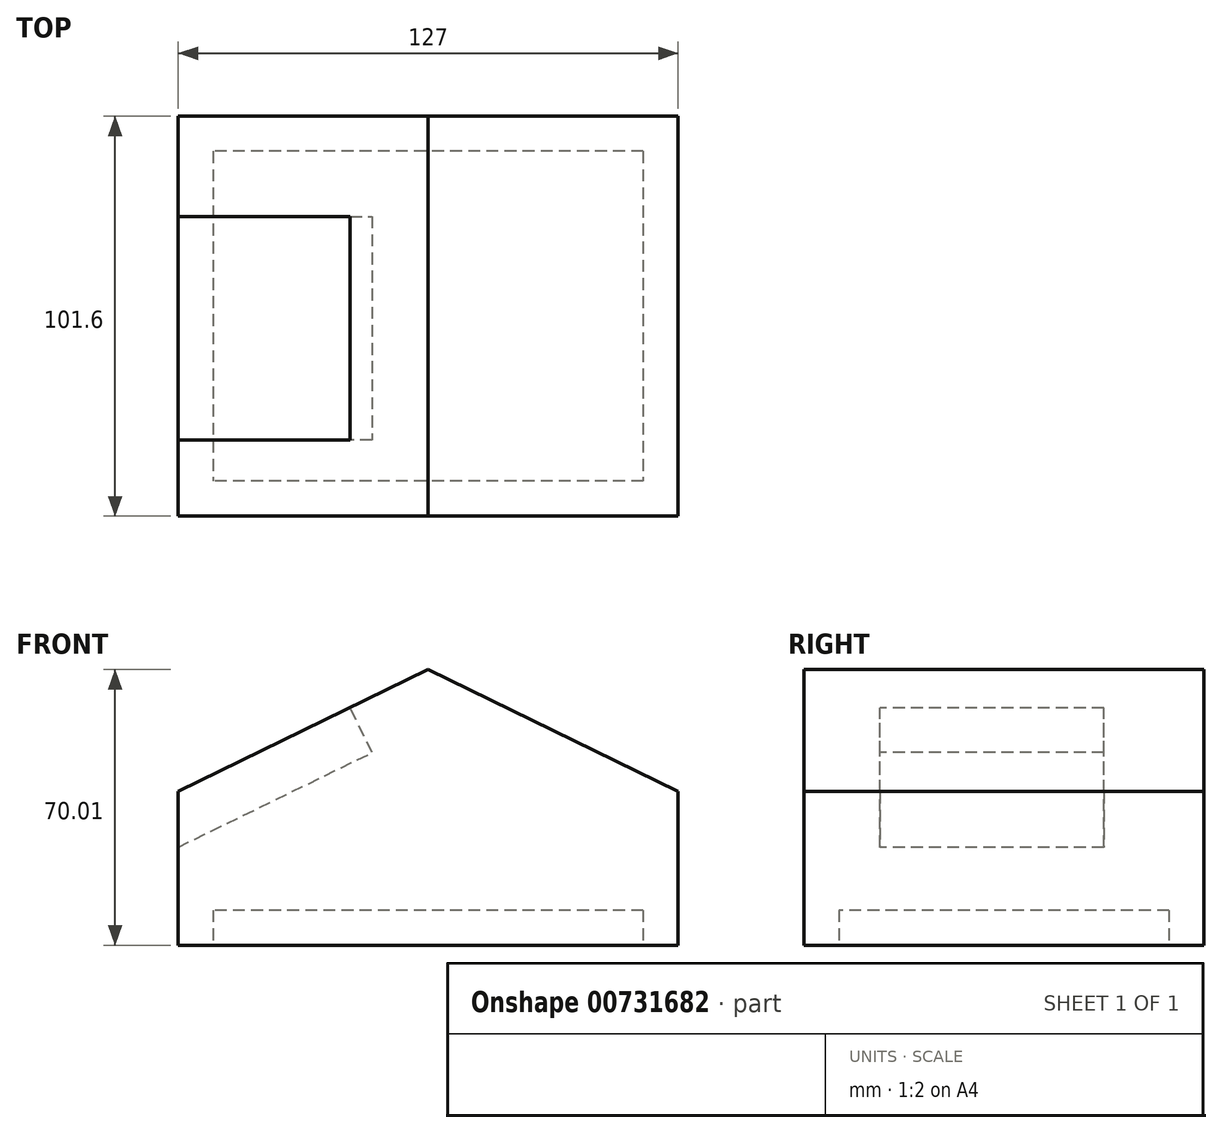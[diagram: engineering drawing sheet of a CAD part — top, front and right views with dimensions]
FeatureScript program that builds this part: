
annotation { "Feature Type Name" : "Feature", "Feature Type Description" : "" }
export const myFeature = defineFeature(function(context is Context, id is Id, definition is map)
    precondition{}
    {
        {
            var Q0;
            Q0=qCreatedBy(makeId("Right.planeOp"),FACE);
            var sketch = newSketch(context, id + "F0", { "sketchPlane" : qUnion([Q0])});
            skLineSegment(sketch, "E0.bottom", {"start": v(-50.24, 20.62) * mm, "end": v(51.36, 20.62) * mm});
            skLineSegment(sketch, "E0.top", {"start": v(-50.24, -55.58) * mm, "end": v(51.36, -55.58) * mm});
            skLineSegment(sketch, "E0.left", {"start": v(-50.24, 20.62) * mm, "end": v(-50.24, -55.58) * mm});
            skLineSegment(sketch, "E0.right", {"start": v(51.36, 20.62) * mm, "end": v(51.36, -55.58) * mm});
            skSolve(sketch);
        }
        {
            var Q0;
            Q0 = qSketchRegion(id + "F0", true);
            var Q1;
            Q1=makeQuery(id+"F0.imprint","IMPRINT",FACE,{"disambiguationData":[TD([[makeQuery(id+"F0.imprint","IMPRINT",EDGE,{"derivedFrom":sQuery(id+"F0.wireOp",EDGE,"E0.bottom")}),-1.0]])]});
            extrude(context, id + "F1", {"entities" : qUnion([Q0, Q1]), "depth" : 127 * mm, "offsetDistance" : 25.4 * mm});
        }
        {
            var Q0;
            Q0=makeQuery(id+"F1.opExtrude","SWEPT_FACE",FACE,{"disambiguationData":[OSD([sQuery(id+"F0.wireOp",EDGE,"E0.bottom")])]});
            var sketch = newSketch(context, id + "F2", { "sketchPlane" : qUnion([Q0])});
            skLineSegment(sketch, "E1.bottom", {"start": v(-50.24, -32.2) * mm, "end": v(51.36, -32.2) * mm});
            skLineSegment(sketch, "E1.top", {"start": v(-50.24, -83) * mm, "end": v(51.36, -83) * mm});
            skLineSegment(sketch, "E1.left", {"start": v(-50.24, -32.2) * mm, "end": v(-50.24, -83) * mm});
            skLineSegment(sketch, "E1.right", {"start": v(51.36, -32.2) * mm, "end": v(51.36, -83) * mm});
            skSolve(sketch);
        }
        {
            var Q0;
            Q0=makeQuery(id+"F1.opExtrude","CAP_EDGE",EDGE,{"disambiguationData":[OSD([sQuery(id+"F0.wireOp",EDGE,"E0.bottom")])],"isStart":true});
            var Q1;
            Q1=makeQuery(id+"F1.opExtrude","CAP_EDGE",EDGE,{"disambiguationData":[OSD([sQuery(id+"F0.wireOp",EDGE,"E0.bottom")])],"isStart":false});
            chamfer(context, id + "F3", {"entities" : qUnion([Q0, Q1]), "chamferType" : ChamferType.OFFSET_ANGLE, "width" : 76.2 * mm, "oppositeDirection" : false, "angle" : 26 * degree, "tangentPropagation" : true});
        }
        {
            var Q0;
            Q0=makeQuery(id+"F1.opExtrude","SWEPT_FACE",FACE,{"disambiguationData":[OSD([sQuery(id+"F0.wireOp",EDGE,"E0.left")])]});
            var sketch = newSketch(context, id + "F4", { "sketchPlane" : qUnion([Q0])});
            skLineSegment(sketch, "E2", {"start": v(84.28, 11.73) * mm, "end": v(112.77, -46.69) * mm});
            skLineSegment(sketch, "E3", {"start": v(112.77, -46.69) * mm, "end": v(14.23, -46.69) * mm});
            skLineSegment(sketch, "E4", {"start": v(14.23, -46.69) * mm, "end": v(42.72, 11.73) * mm});
            skLineSegment(sketch, "E5", {"start": v(42.72, 11.73) * mm, "end": v(84.28, 11.73) * mm});
            skSolve(sketch);
        }
        {
            var Q0;
            Q0=makeQuery(id+"F4.imprint","IMPRINT",FACE,{"disambiguationData":[TD([[makeQuery(id+"F4.imprint","IMPRINT",EDGE,{"derivedFrom":sQuery(id+"F4.wireOp",EDGE,"E2")}),-1.0]])]});
            extrude(context, id + "F5", {"entities" : qUnion([Q0]), "operationType" : NewBodyOperationType.REMOVE, "oppositeDirection" : true, "depth" : 127 * mm, "offsetDistance" : 25.4 * mm});
        }
        {
            var Q0;
            {var subQ0=sQuery(id+"F0.wireOp",EDGE,"E0.bottom");Q0=makeQuery(id+"F3.opChamfer","BLEND_FACE",FACE,{"disambiguationData":[OSD([subQ0]),TDD([makeQuery(id+"F1.opExtrude","CAP_EDGE",EDGE,{"disambiguationData":[OSD([subQ0])],"isStart":true})])]});}
            var sketch = newSketch(context, id + "F6", { "sketchPlane" : qUnion([Q0])});
            skLineSegment(sketch, "E6.bottom", {"start": v(-42.47, 25.94) * mm, "end": v(41.35, 25.94) * mm});
            skLineSegment(sketch, "E6.top", {"start": v(-42.47, -30.9) * mm, "end": v(41.35, -30.9) * mm});
            skLineSegment(sketch, "E6.left", {"start": v(-42.47, 25.94) * mm, "end": v(-42.47, -30.9) * mm});
            skLineSegment(sketch, "E6.right", {"start": v(41.35, 25.94) * mm, "end": v(41.35, -30.9) * mm});
            skSolve(sketch);
        }
        {
            var Q0;
            Q0=makeQuery(id+"F6.imprint","IMPRINT",FACE,{"disambiguationData":[TD([[makeQuery(id+"F6.imprint","IMPRINT",EDGE,{"derivedFrom":sQuery(id+"F6.wireOp",EDGE,"E6.bottom")}),-1.0]])]});
            extrude(context, id + "F7", {"entities" : qUnion([Q0]), "operationType" : NewBodyOperationType.REMOVE, "oppositeDirection" : true, "depth" : 12.7 * mm, "offsetDistance" : 25.4 * mm});
        }
        {
            var Q0;
            {var subQ0=sQuery(id+"F0.wireOp",EDGE,"E0.bottom");Q0=makeQuery(id+"F3.opChamfer","BLEND_FACE",FACE,{"disambiguationData":[OSD([subQ0]),TDD([makeQuery(id+"F1.opExtrude","CAP_EDGE",EDGE,{"disambiguationData":[OSD([subQ0])],"isStart":false})])]});}
            var sketch = newSketch(context, id + "F8", { "sketchPlane" : qUnion([Q0])});
            skLineSegment(sketch, "E7.bottom", {"start": v(-41.35, -29.74) * mm, "end": v(42.47, -29.74) * mm});
            skLineSegment(sketch, "E7.top", {"start": v(-41.35, -86.58) * mm, "end": v(42.47, -86.58) * mm});
            skLineSegment(sketch, "E7.left", {"start": v(-41.35, -29.74) * mm, "end": v(-41.35, -86.58) * mm});
            skLineSegment(sketch, "E7.right", {"start": v(42.47, -29.74) * mm, "end": v(42.47, -86.58) * mm});
            skSolve(sketch);
        }
        {
            var Q0;
            Q0=makeQuery(id+"F8.imprint","IMPRINT",FACE,{"disambiguationData":[TD([[makeQuery(id+"F8.imprint","IMPRINT",EDGE,{"derivedFrom":sQuery(id+"F8.wireOp",EDGE,"E7.bottom")}),-1.0]])]});
            extrude(context, id + "F9", {"entities" : qUnion([Q0]), "operationType" : NewBodyOperationType.REMOVE, "oppositeDirection" : true, "depth" : 10.16 * mm, "offsetDistance" : 25.4 * mm});
        }
        {
            var Q0;
            Q0=makeQuery(id+"F1.opExtrude","SWEPT_FACE",FACE,{"disambiguationData":[OSD([sQuery(id+"F0.wireOp",EDGE,"E0.top")])]});
            var sketch = newSketch(context, id + "F10", { "sketchPlane" : qUnion([Q0])});
            skLineSegment(sketch, "E8.bottom", {"start": v(42.47, 118.11) * mm, "end": v(-41.35, 118.11) * mm});
            skLineSegment(sketch, "E8.top", {"start": v(42.47, 8.9) * mm, "end": v(-41.35, 8.89) * mm});
            skLineSegment(sketch, "E8.left", {"start": v(42.47, 118.11) * mm, "end": v(42.47, 8.9) * mm});
            skLineSegment(sketch, "E8.right", {"start": v(-41.35, 118.11) * mm, "end": v(-41.35, 8.89) * mm});
            skSolve(sketch);
        }
        {
            var Q0;
            Q0=makeQuery(id+"F10.imprint","IMPRINT",FACE,{"disambiguationData":[TD([[makeQuery(id+"F10.imprint","IMPRINT",EDGE,{"derivedFrom":sQuery(id+"F10.wireOp",EDGE,"E8.bottom")}),1.0]])]});
            extrude(context, id + "F11", {"entities" : qUnion([Q0]), "operationType" : NewBodyOperationType.REMOVE, "oppositeDirection" : true, "depth" : 8.9 * mm, "offsetDistance" : 25.4 * mm});
        }
        {
            var Q0;
            Q0=makeQuery(id+"F1.opExtrude","SWEPT_FACE",FACE,{"disambiguationData":[OSD([sQuery(id+"F0.wireOp",EDGE,"E0.top")])]});
            var sketch = newSketch(context, id + "F12", { "sketchPlane" : qUnion([Q0])});
            skLineSegment(sketch, "E9.bottom", {"start": v(118.11, -42.47) * mm, "end": v(8.9, -42.47) * mm});
            skLineSegment(sketch, "E9.top", {"start": v(118.11, 41.35) * mm, "end": v(8.89, 41.35) * mm});
            skLineSegment(sketch, "E9.left", {"start": v(118.11, -42.47) * mm, "end": v(118.11, 41.35) * mm});
            skLineSegment(sketch, "E9.right", {"start": v(8.9, -42.47) * mm, "end": v(8.89, 41.35) * mm});
            skSolve(sketch);
        }
        {
            var Q0;
            Q0=makeQuery(id+"F12.imprint","IMPRINT",FACE,{"disambiguationData":[TD([[makeQuery(id+"F12.imprint","IMPRINT",EDGE,{"derivedFrom":sQuery(id+"F12.wireOp",EDGE,"E9.bottom")}),-1.0]])]});
            extrude(context, id + "F13", {"entities" : qUnion([Q0]), "operationType" : NewBodyOperationType.REMOVE, "oppositeDirection" : true, "depth" : 8.9 * mm, "offsetDistance" : 25.4 * mm});
        }
    });
